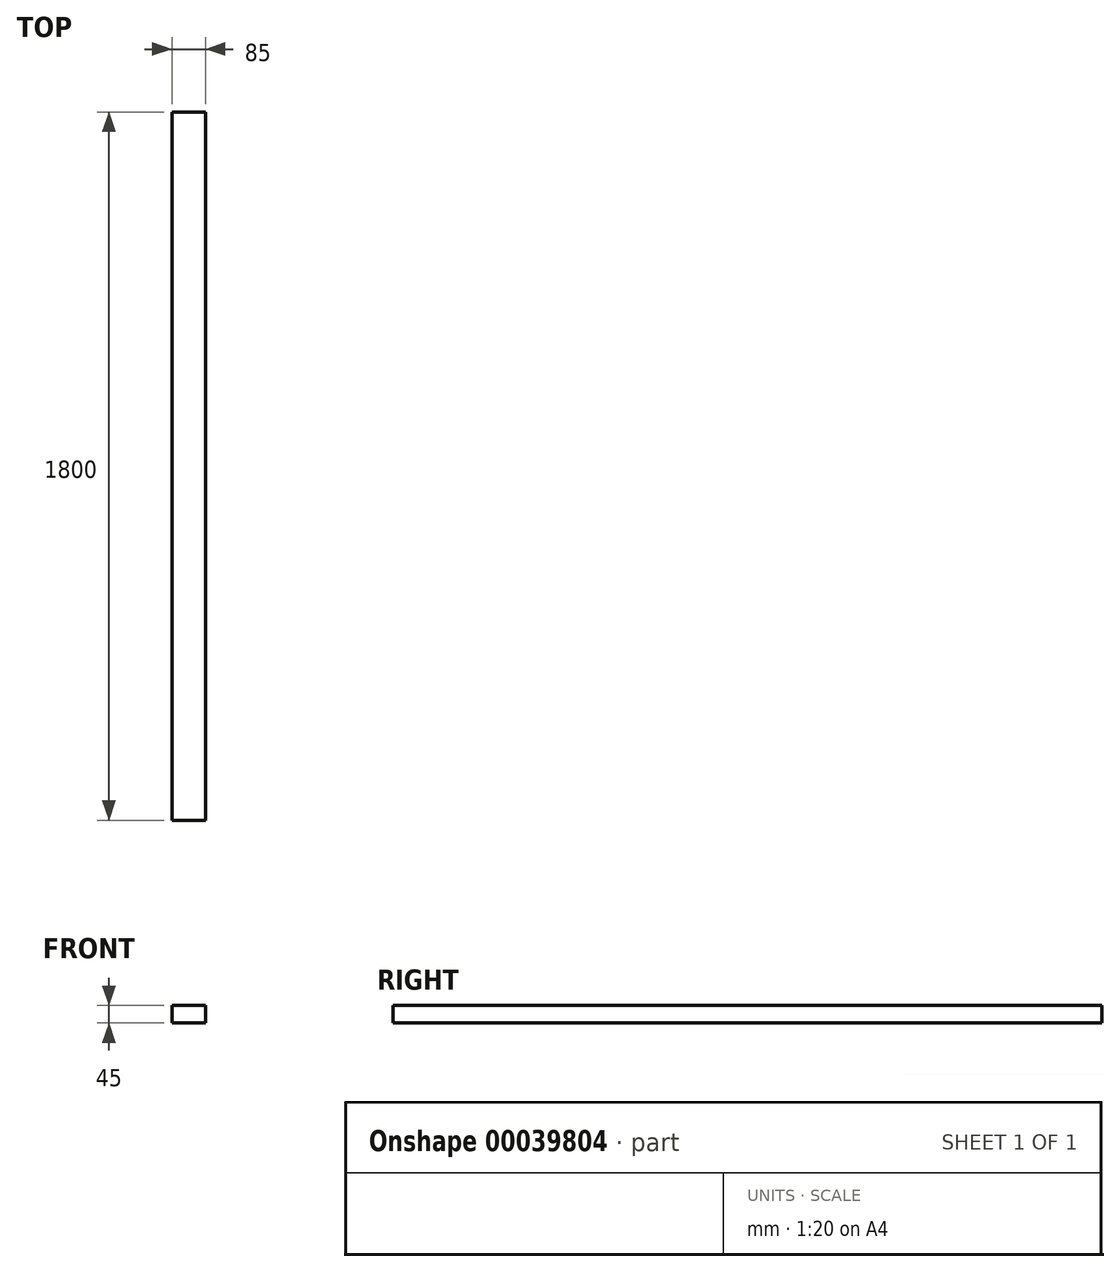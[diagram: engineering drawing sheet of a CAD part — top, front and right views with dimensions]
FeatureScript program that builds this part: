
annotation { "Feature Type Name" : "Feature", "Feature Type Description" : "" }
export const myFeature = defineFeature(function(context is Context, id is Id, definition is map)
    precondition{}
    {
        {
            var Q0;
            Q0=qCreatedBy(makeId("Front.planeOp"),FACE);
            var sketch = newSketch(context, id + "F0", { "sketchPlane" : qUnion([Q0])});
            skLineSegment(sketch, "E0.rect.bottom", {"start": v(42.5, -22.5) * mm, "end": v(-42.5, -22.5) * mm});
            skLineSegment(sketch, "E0.rect.top", {"start": v(42.5, 22.5) * mm, "end": v(-42.5, 22.5) * mm});
            skLineSegment(sketch, "E0.rect.left", {"start": v(42.5, -22.5) * mm, "end": v(42.5, 22.5) * mm});
            skLineSegment(sketch, "E0.rect.right", {"start": v(-42.5, -22.5) * mm, "end": v(-42.5, 22.5) * mm});
            skPoint(sketch, "E0.rect.middle", {"position": v(0, 0) * mm});
            skSolve(sketch);
        }
        {
            var Q0;
            Q0=qSketchRegion(id+"F0",true);
            extrude(context, id + "F1", {"entities" : qUnion([Q0]), "depth" : 1800 * mm});
        }
    });
